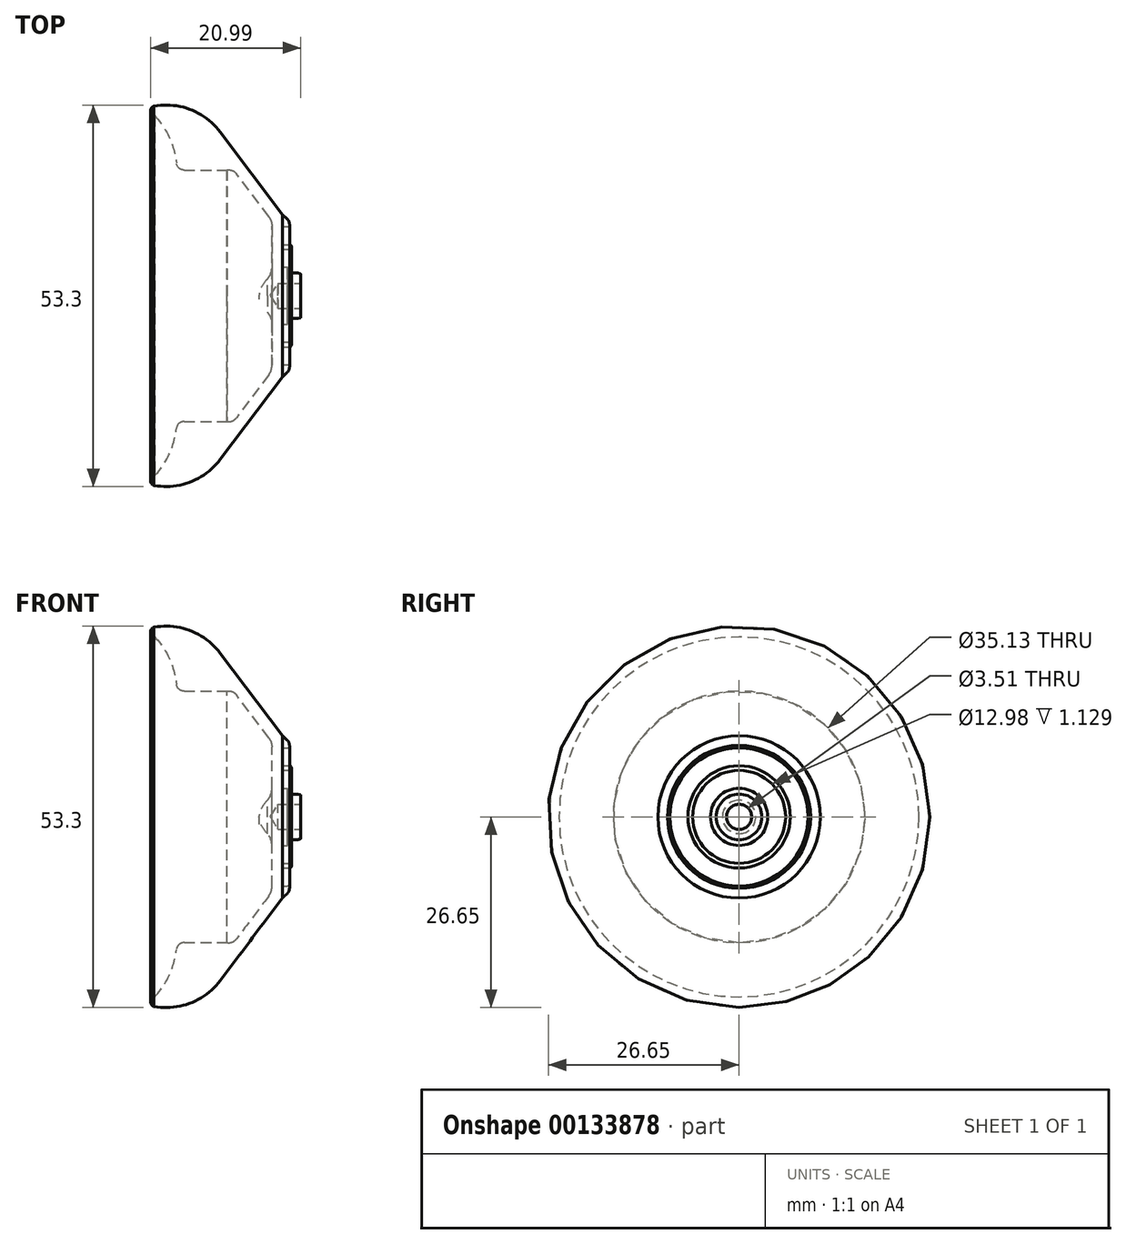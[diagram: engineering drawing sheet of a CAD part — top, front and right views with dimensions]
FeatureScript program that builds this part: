
annotation { "Feature Type Name" : "Feature", "Feature Type Description" : "" }
export const myFeature = defineFeature(function(context is Context, id is Id, definition is map)
    precondition{}
    {
        {
            var Q0;
            Q0=qCreatedBy(makeId("Front.planeOp"),FACE);
            var sketch = newSketch(context, id + "F0", { "sketchPlane" : qUnion([Q0])});
            skPoint(sketch, "E0.visualSharp", {"position": v(-2.1, 3.02) * mm});
            skLineSegment(sketch, "E1", {"start": v(2.35, 10.72) * mm, "end": v(1.67, 11.34) * mm});
            skPoint(sketch, "E2.visualSharp", {"position": v(2.67, 10.42) * mm});
            skArc(sketch, "E2.filletArc", {"start": v(2.67, 9.98) * mm, "mid": v(2.59, 10.38) * mm, "end": v(2.35, 10.72) * mm});
            skPoint(sketch, "E3.startSnap0", {"position": v(-6.46, 26.5) * mm});
            skLineSegment(sketch, "E4", {"start": v(0.21, 4.02) * mm, "end": v(0.21, 9.73) * mm});
            skPoint(sketch, "E5.visualSharp", {"position": v(-16.77, 26.5) * mm});
            skPoint(sketch, "E6.visualSharp", {"position": v(-16.77, 25.5) * mm});
            skPoint(sketch, "E7.visualSharp", {"position": v(-6.46, 20.31) * mm});
            skPoint(sketch, "E8.visualSharp", {"position": v(0.21, 10.47) * mm});
            skArc(sketch, "E8.filletArc", {"start": v(0.21, 9.73) * mm, "mid": v(0.1, 10.43) * mm, "end": v(-0.23, 11.06) * mm});
            skPoint(sketch, "E9.visualSharp", {"position": v(-5.14, 17.59) * mm});
            skPoint(sketch, "E10.visualSharp", {"position": v(-5.46, 18.02) * mm});
            skPoint(sketch, "E11.visualSharp", {"position": v(-4.4, 16.61) * mm});
            skLineSegment(sketch, "E12", {"start": v(4.25, 1.75) * mm, "end": v(1.05, 1.75) * mm});
            skArc(sketch, "E13", {"start": v(2.42, 9.65) * mm, "mid": v(2.6, 9.73) * mm, "end": v(2.67, 9.9) * mm});
            skLineSegment(sketch, "E14", {"start": v(1.67, 7.15) * mm, "end": v(1.67, 9.65) * mm});
            skLineSegment(sketch, "E15", {"start": v(1.67, 9.65) * mm, "end": v(2.42, 9.65) * mm});
            skLineSegment(sketch, "E16", {"start": v(2.93, 6.62) * mm, "end": v(2.93, 6.9) * mm});
            skLineSegment(sketch, "E17", {"start": v(1.05, 1.75) * mm, "end": v(0, 0) * mm});
            skArc(sketch, "E18", {"start": v(2.93, 6.9) * mm, "mid": v(2.85, 7.08) * mm, "end": v(2.67, 7.15) * mm});
            skArc(sketch, "E19", {"start": v(2.8, 6.5) * mm, "mid": v(2.9, 6.53) * mm, "end": v(2.93, 6.62) * mm});
            skLineSegment(sketch, "E20", {"start": v(1.67, 6.5) * mm, "end": v(2.8, 6.5) * mm});
            skLineSegment(sketch, "E21", {"start": v(1.67, 4) * mm, "end": v(1.67, 6.5) * mm});
            skLineSegment(sketch, "E22", {"start": v(1.67, 4) * mm, "end": v(2.37, 4) * mm});
            skLineSegment(sketch, "E23", {"start": v(4.25, 1.75) * mm, "end": v(4.25, 2.97) * mm});
            skLineSegment(sketch, "E24", {"start": v(2.37, 3.19) * mm, "end": v(2.37, 4) * mm});
            skLineSegment(sketch, "E25", {"start": v(4.16, 3.09) * mm, "end": v(3.88, 3.18) * mm});
            skLineSegment(sketch, "E26", {"start": v(2.37, 3.19) * mm, "end": v(3.84, 3.19) * mm});
            skLineSegment(sketch, "E27", {"start": v(1.67, 7.15) * mm, "end": v(2.67, 7.15) * mm});
            skArc(sketch, "E28", {"start": v(4.25, 2.97) * mm, "mid": v(4.22, 3.04) * mm, "end": v(4.16, 3.09) * mm});
            skArc(sketch, "E29", {"start": v(3.88, 3.18) * mm, "mid": v(3.86, 3.18) * mm, "end": v(3.84, 3.19) * mm});
            skLineSegment(sketch, "E30", {"start": v(0, 0) * mm, "end": v(-1.6, 0) * mm});
            skLineSegment(sketch, "E31", {"start": v(2.67, 9.98) * mm, "end": v(2.67, 9.9) * mm});
            skArc(sketch, "E32", {"start": v(-0.4, 2.34) * mm, "mid": v(0.05, 3.12) * mm, "end": v(0.21, 4.02) * mm});
            skPoint(sketch, "E33.visualSharp", {"position": v(-1.12, 1.75) * mm});
            skArc(sketch, "E34", {"start": v(-0.4, 2.34) * mm, "mid": v(-1.2, 1.27) * mm, "end": v(-1.6, 0) * mm});
            skLineSegment(sketch, "E35", {"start": v(-0.23, 11.06) * mm, "end": v(-4.73, 17.04) * mm});
            skArc(sketch, "E36.filletArc", {"start": v(-4.73, 17.04) * mm, "mid": v(-5.33, 17.5) * mm, "end": v(-6.07, 17.56) * mm});
            skLineSegment(sketch, "E37", {"start": v(1.67, 11.34) * mm, "end": v(-6.99, 22.85) * mm});
            skArc(sketch, "E38", {"start": v(-6.99, 22.85) * mm, "mid": v(-11.1, 25.99) * mm, "end": v(-16.25, 26.5) * mm});
            skLineSegment(sketch, "E39", {"start": v(-6.07, 17.56) * mm, "end": v(-12.04, 17.56) * mm});
            skArc(sketch, "E40", {"start": v(-13.14, 18.55) * mm, "mid": v(-14.1, 22.1) * mm, "end": v(-16.16, 25.14) * mm});
            skPoint(sketch, "E41.visualSharp", {"position": v(-13.08, 17.56) * mm});
            skArc(sketch, "E41.filletArc", {"start": v(-13.14, 18.55) * mm, "mid": v(-12.78, 17.85) * mm, "end": v(-12.04, 17.56) * mm});
            skArc(sketch, "E42", {"start": v(-16.25, 26.5) * mm, "mid": v(-16.74, 25.78) * mm, "end": v(-16.16, 25.14) * mm});
            skSolve(sketch);
        }
        {
            var Q0;
            Q0=makeQuery(id+"F0.imprint","IMPRINT",FACE,{"disambiguationData":[TD([[makeQuery(id+"F0.imprint","IMPRINT",EDGE,{"derivedFrom":sQuery(id+"F0.wireOp",EDGE,"E1")}),1.0]])]});
            var Q1;
            Q1=sQuery(id+"F0.wireOp",EDGE,"E30");
            revolve(context, id + "F1", {"entities" : qUnion([Q0]), "axis" : qUnion([Q1]), "revolveType" : RevolveType.FULL});
        }
    });
